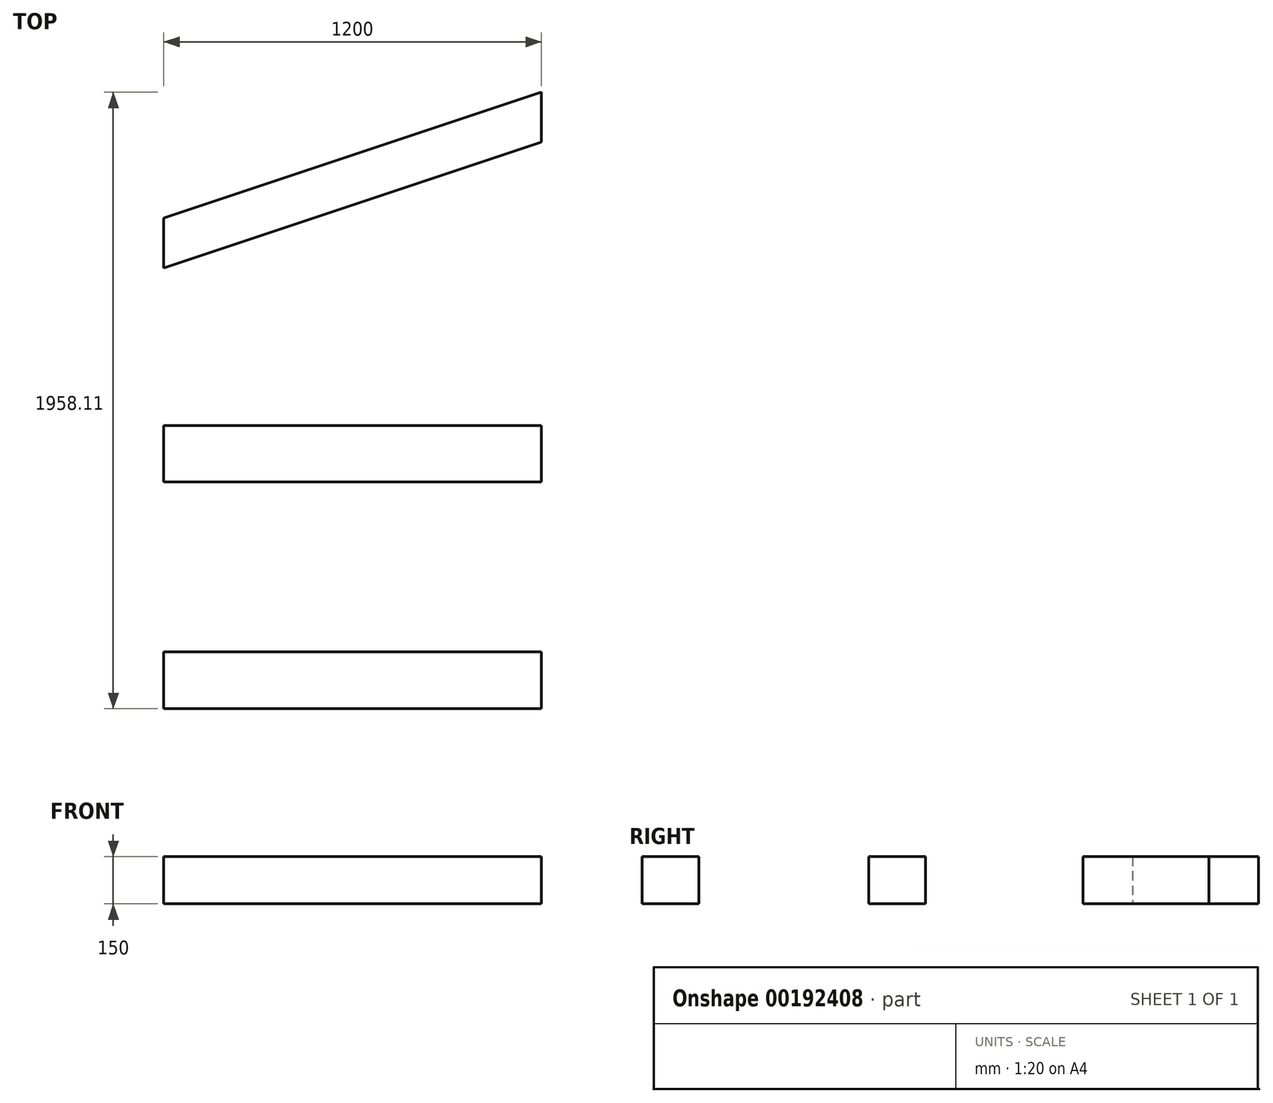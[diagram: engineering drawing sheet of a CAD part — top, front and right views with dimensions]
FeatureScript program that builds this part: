
annotation { "Feature Type Name" : "Feature", "Feature Type Description" : "" }
export const myFeature = defineFeature(function(context is Context, id is Id, definition is map)
    precondition{}
    {
        {
            var Q0;
            Q0=qCreatedBy(makeId("Top.planeOp"),FACE);
            var sketch = newSketch(context, id + "F0", { "sketchPlane" : qUnion([Q0])});
            skLineSegment(sketch, "E0.bottom", {"start": v(0, 0) * mm, "end": v(1200, 0) * mm});
            skLineSegment(sketch, "E0.top", {"start": v(0, -180) * mm, "end": v(1200, -180) * mm});
            skLineSegment(sketch, "E0.left", {"start": v(0, 0) * mm, "end": v(0, -180) * mm});
            skLineSegment(sketch, "E0.right", {"start": v(1200, 0) * mm, "end": v(1200, -180) * mm});
            skLineSegment(sketch, "E1.bottom", {"start": v(0, 720) * mm, "end": v(1200, 720) * mm});
            skLineSegment(sketch, "E1.top", {"start": v(0, 540) * mm, "end": v(1200, 540) * mm});
            skLineSegment(sketch, "E1.left", {"start": v(0, 720) * mm, "end": v(0, 540) * mm});
            skLineSegment(sketch, "E1.right", {"start": v(1200, 720) * mm, "end": v(1200, 540) * mm});
            skLineSegment(sketch, "E2", {"start": v(0, 1378.11) * mm, "end": v(1200, 1778.11) * mm});
            skLineSegment(sketch, "E3", {"start": v(1200, 1620) * mm, "end": v(1200, 1778.11) * mm});
            skLineSegment(sketch, "E4", {"start": v(1200, 1620) * mm, "end": v(0, 1220) * mm});
            skLineSegment(sketch, "E5", {"start": v(0, 1378.11) * mm, "end": v(0, 1220) * mm});
            skSolve(sketch);
        }
        {
            var Q0;
            Q0=makeQuery(id+"F0.imprint","IMPRINT",FACE,{"disambiguationData":[TD([[makeQuery(id+"F0.imprint","IMPRINT",EDGE,{"derivedFrom":sQuery(id+"F0.wireOp",EDGE,"E2")}),-1.0]])]});
            var Q1;
            Q1=makeQuery(id+"F0.imprint","IMPRINT",FACE,{"disambiguationData":[TD([[makeQuery(id+"F0.imprint","IMPRINT",EDGE,{"derivedFrom":sQuery(id+"F0.wireOp",EDGE,"E1.bottom")}),-1.0]])]});
            var Q2;
            Q2=makeQuery(id+"F0.imprint","IMPRINT",FACE,{"disambiguationData":[TD([[makeQuery(id+"F0.imprint","IMPRINT",EDGE,{"derivedFrom":sQuery(id+"F0.wireOp",EDGE,"E0.bottom")}),-1.0]])]});
            extrude(context, id + "F1", {"entities" : qUnion([Q0, Q1, Q2]), "depth" : 150 * mm});
        }
    });
